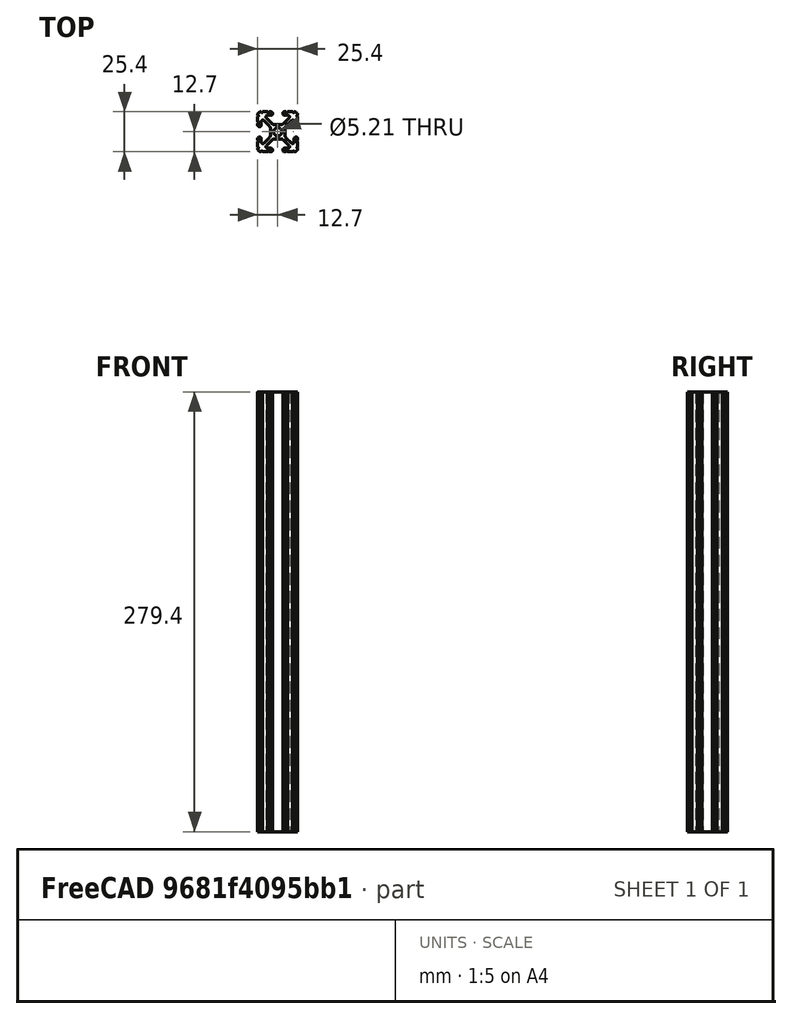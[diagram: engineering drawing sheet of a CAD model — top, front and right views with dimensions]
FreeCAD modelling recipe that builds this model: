
FCSTD DOCUMENT  (FreeCAD 0.19R24267 (Git))
Label: 1010-11
License: All rights reserved
LicenseURL: http://en.wikipedia.org/wiki/All_rights_reserved
objects: Sketcher::SketchObject×1, Part::Extrusion×1
note: 2 computed .brp shape members not serialized (recipe doc carries the construction recipe); baked Part::Feature solids carry a one-line shape summary decoded from their .brp

FEATURE [Sketcher::SketchObject] Sketch097
  FullyConstrained = false
  sketch-geometry (97):
    g0: Circle CenterX=0 CenterY=0 CenterZ=0 NormalX=0 NormalY=0 NormalZ=-1 AngleXU=0 Radius=2.6035
    g1: ArcOfCircle CenterX=12.7 CenterY=5.82508 CenterZ=0 NormalX=0 NormalY=0 NormalZ=1 AngleXU=0 Radius=0.508 StartAngle=1.5708 EndAngle=4.71239
    g2: LineSegment StartX=3.2385 StartY=11.651 StartZ=0 EndX=3.2385 EndY=11.5392 EndZ=0
    g3: LineSegment StartX=6.33313 StartY=-12.7 StartZ=0 EndX=9.55044 EndY=-12.7 EndZ=0
    g4: LineSegment StartX=7.20704 StartY=8.72437 StartZ=0 EndX=3.89827 EndY=5.42317 EndZ=0
    g5: ArcOfCircle CenterX=7.6835 CenterY=1.59319 CenterZ=0 NormalX=0 NormalY=0 NormalZ=1 AngleXU=0 Radius=3.175 StartAngle=2.35505 EndAngle=3.14159
    g6: ArcOfCircle CenterX=-1.70925 CenterY=-7.6708 CenterZ=0 NormalX=0 NormalY=0 NormalZ=1 AngleXU=0 Radius=3.175 StartAngle=1.5708 EndAngle=2.35528
    g7: ArcOfCircle CenterX=11.5392 CenterY=-4.28747 CenterZ=0 NormalX=0 NormalY=0 NormalZ=1 AngleXU=0 Radius=1.04901 StartAngle=1.5708 EndAngle=3.14159
    g8: ArcOfCircle CenterX=12.7 CenterY=-5.82508 CenterZ=0 NormalX=0 NormalY=0 NormalZ=1 AngleXU=0 Radius=0.508 StartAngle=1.5708 EndAngle=4.71239
    g9: LineSegment StartX=4.28751 StartY=10.4902 StartZ=0 EndX=6.47679 EndY=10.4902 EndZ=0
    g10: ArcOfCircle CenterX=4.28751 CenterY=11.651 CenterZ=0 NormalX=0 NormalY=0 NormalZ=1 AngleXU=0 Radius=1.04901 StartAngle=1.5708 EndAngle=3.14159
    g11: ArcOfCircle CenterX=6.47679 CenterY=9.45629 CenterZ=0 NormalX=0 NormalY=0 NormalZ=1 AngleXU=0 Radius=1.03391 StartAngle=5.49664 EndAngle=7.85398
    g12: ArcOfCircle CenterX=4.28751 CenterY=11.5392 CenterZ=0 NormalX=0 NormalY=0 NormalZ=1 AngleXU=0 Radius=1.04901 StartAngle=3.14159 EndAngle=4.71239
    g13: LineSegment StartX=3.95227 StartY=-5.42369 StartZ=0 EndX=7.17965 EndY=-8.64519 EndZ=0
    g14: ArcOfCircle CenterX=11.651 CenterY=4.28747 CenterZ=0 NormalX=0 NormalY=0 NormalZ=1 AngleXU=0 Radius=1.04901 StartAngle=4.71239 EndAngle=6.28319
    g15: ArcOfCircle CenterX=-5.82513 CenterY=-12.7 CenterZ=0 NormalX=0 NormalY=0 NormalZ=1 AngleXU=0 Radius=0.508 StartAngle=0 EndAngle=3.14159
    g16: LineSegment StartX=-6.47679 StartY=10.4902 StartZ=0 EndX=-4.28751 EndY=10.4902 EndZ=0
    g17: ArcOfCircle CenterX=-12.7 CenterY=10.0584 CenterZ=0 NormalX=0 NormalY=0 NormalZ=1 AngleXU=0 Radius=0.508 StartAngle=4.71239 EndAngle=7.85368
    g18: ArcOfCircle CenterX=-12.7 CenterY=5.82508 CenterZ=0 NormalX=0 NormalY=0 NormalZ=1 AngleXU=0 Radius=0.508 StartAngle=4.71239 EndAngle=7.85398
    g19: LineSegment StartX=-11.5392 StartY=-3.23846 StartZ=0 EndX=-11.651 EndY=-3.23846 EndZ=0
    g20: LineSegment StartX=-3.89827 StartY=5.42317 StartZ=0 EndX=-7.20704 EndY=8.72437 EndZ=0
    g21: LineSegment StartX=1.65578 StartY=4.4958 StartZ=0 EndX=-1.65578 EndY=4.4958 EndZ=0
    g22: ArcOfCircle CenterX=-1.65578 CenterY=7.6708 CenterZ=0 NormalX=0 NormalY=0 NormalZ=1 AngleXU=0 Radius=3.175 StartAngle=3.92813 EndAngle=4.71239
    g23: LineSegment StartX=-9.55044 StartY=-12.7 StartZ=0 EndX=-6.33313 EndY=-12.7 EndZ=0
    g24: ArcOfCircle CenterX=-5.82513 CenterY=12.7 CenterZ=0 NormalX=0 NormalY=0 NormalZ=1 AngleXU=0 Radius=0.508 StartAngle=3.14159 EndAngle=6.28319
    g25: ArcOfCircle CenterX=-4.28751 CenterY=11.651 CenterZ=0 NormalX=0 NormalY=0 NormalZ=1 AngleXU=0 Radius=1.04901 StartAngle=0 EndAngle=1.5708
    g26: LineSegment StartX=-12.7 StartY=-4.28747 StartZ=0 EndX=-12.7 EndY=-5.31708 EndZ=0
    g27: ArcOfCircle CenterX=-6.47679 CenterY=9.45629 CenterZ=0 NormalX=0 NormalY=0 NormalZ=1 AngleXU=0 Radius=1.03391 StartAngle=1.5708 EndAngle=3.92813
    g28: ArcOfCircle CenterX=-4.28751 CenterY=11.5392 CenterZ=0 NormalX=0 NormalY=0 NormalZ=1 AngleXU=0 Radius=1.04901 StartAngle=4.71239 EndAngle=6.28319
    g29: LineSegment StartX=-5.44101 StartY=-3.84082 StartZ=0 EndX=-8.73713 EndY=-7.12941 EndZ=0
    g30: ArcOfCircle CenterX=-7.6835 CenterY=-1.59319 CenterZ=0 NormalX=0 NormalY=0 NormalZ=1 AngleXU=0 Radius=3.175 StartAngle=5.49664 EndAngle=6.28319
    g31: LineSegment StartX=-12.7 StartY=5.31708 StartZ=0 EndX=-12.7 EndY=4.28747 EndZ=0
    g32: LineSegment StartX=-8.73713 StartY=7.12941 StartZ=0 EndX=-5.44101 EndY=3.84082 EndZ=0
    g33: LineSegment StartX=-11.651 StartY=3.23846 StartZ=0 EndX=-11.5392 EndY=3.23846 EndZ=0
    g34: ArcOfCircle CenterX=-9.46279 CenterY=-6.40209 CenterZ=0 NormalX=0 NormalY=0 NormalZ=1 AngleXU=0 Radius=1.02741 StartAngle=3.14159 EndAngle=5.49664
    g35: ArcOfCircle CenterX=-10.5918 CenterY=10.5918 CenterZ=0 NormalX=0 NormalY=0 NormalZ=1 AngleXU=0 Radius=2.1082 StartAngle=1.55877 EndAngle=3.15364
    g36: LineSegment StartX=-12.7 StartY=9.5504 StartZ=0 EndX=-12.7 EndY=6.33308 EndZ=0
    g37: LineSegment StartX=-6.33313 StartY=12.7 StartZ=0 EndX=-9.55044 EndY=12.7 EndZ=0
    g38: ArcOfCircle CenterX=-11.5392 CenterY=-4.28747 CenterZ=0 NormalX=0 NormalY=0 NormalZ=1 AngleXU=0 Radius=1.04901 StartAngle=0 EndAngle=1.5708
    g39: LineSegment StartX=4.28751 StartY=-12.7 StartZ=0 EndX=5.31713 EndY=-12.7 EndZ=0
    g40: LineSegment StartX=5.44101 StartY=3.84082 StartZ=0 EndX=8.73713 EndY=7.12941 EndZ=0
    g41: LineSegment StartX=10.4902 StartY=-4.28747 StartZ=0 EndX=10.4902 EndY=-6.40209 EndZ=0
    g42: ArcOfCircle CenterX=9.46279 CenterY=6.40209 CenterZ=0 NormalX=0 NormalY=0 NormalZ=1 AngleXU=0 Radius=1.02741 StartAngle=0 EndAngle=2.35505
    g43: ArcOfCircle CenterX=5.82513 CenterY=-12.7 CenterZ=0 NormalX=0 NormalY=0 NormalZ=1 AngleXU=0 Radius=0.508 StartAngle=0 EndAngle=3.14159
    g44: LineSegment StartX=12.7 StartY=-9.5504 StartZ=0 EndX=12.7 EndY=-6.33308 EndZ=0
    g45: LineSegment StartX=4.5085 StartY=-1.59319 StartZ=0 EndX=4.5085 EndY=1.59319 EndZ=0
    g46: ArcOfCircle CenterX=12.7 CenterY=10.0584 CenterZ=0 NormalX=0 NormalY=0 NormalZ=1 AngleXU=0 Radius=0.508 StartAngle=1.5711 EndAngle=4.71239
    g47: ArcOfCircle CenterX=12.7 CenterY=-10.0584 CenterZ=0 NormalX=0 NormalY=0 NormalZ=1 AngleXU=0 Radius=0.508 StartAngle=1.5708 EndAngle=4.71209
    g48: LineSegment StartX=3.2385 StartY=-11.5392 StartZ=0 EndX=3.2385 EndY=-11.651 EndZ=0
    g49: LineSegment StartX=8.73713 StartY=-7.12941 StartZ=0 EndX=5.44101 EndY=-3.84082 EndZ=0
    g50: ArcOfCircle CenterX=11.651 CenterY=-4.28747 CenterZ=0 NormalX=0 NormalY=0 NormalZ=1 AngleXU=0 Radius=1.04901 StartAngle=0 EndAngle=1.5708
    g51: ArcOfCircle CenterX=1.65578 CenterY=7.6708 CenterZ=0 NormalX=0 NormalY=0 NormalZ=1 AngleXU=0 Radius=3.175 StartAngle=4.71239 EndAngle=5.49664
    g52: ArcOfCircle CenterX=7.6835 CenterY=-1.59319 CenterZ=0 NormalX=0 NormalY=0 NormalZ=1 AngleXU=0 Radius=3.175 StartAngle=3.14159 EndAngle=3.92813
    g53: LineSegment StartX=12.7 StartY=4.28747 StartZ=0 EndX=12.7 EndY=5.31708 EndZ=0
    g54: ArcOfCircle CenterX=6.41641 CenterY=-9.40983 CenterZ=0 NormalX=0 NormalY=0 NormalZ=1 AngleXU=0 Radius=1.08037 StartAngle=4.71239 EndAngle=7.06949
    g55: LineSegment StartX=12.7 StartY=-5.31708 StartZ=0 EndX=12.7 EndY=-4.28747 EndZ=0
    g56: ArcOfCircle CenterX=10.0584 CenterY=-12.7 CenterZ=0 NormalX=0 NormalY=0 NormalZ=1 AngleXU=0 Radius=0.508 StartAngle=0.000300194 EndAngle=3.14159
    g57: ArcOfCircle CenterX=11.5392 CenterY=4.28747 CenterZ=0 NormalX=0 NormalY=0 NormalZ=1 AngleXU=0 Radius=1.04901 StartAngle=3.14159 EndAngle=4.71239
    g58: LineSegment StartX=12.7 StartY=6.33308 StartZ=0 EndX=12.7 EndY=9.5504 EndZ=0
    g59: ArcOfCircle CenterX=4.28751 CenterY=-11.5392 CenterZ=0 NormalX=0 NormalY=0 NormalZ=1 AngleXU=0 Radius=1.04901 StartAngle=1.5708 EndAngle=3.14159
    g60: ArcOfCircle CenterX=10.5918 CenterY=10.5918 CenterZ=0 NormalX=0 NormalY=0 NormalZ=1 AngleXU=0 Radius=2.1082 StartAngle=6.27114 EndAngle=7.86601
    g61: ArcOfCircle CenterX=9.46279 CenterY=-6.40209 CenterZ=0 NormalX=0 NormalY=0 NormalZ=1 AngleXU=0 Radius=1.02741 StartAngle=3.92813 EndAngle=6.28319
    g62: LineSegment StartX=6.41641 StartY=-10.4902 StartZ=0 EndX=4.28751 EndY=-10.4902 EndZ=0
    g63: LineSegment StartX=-10.4902 StartY=-6.40209 StartZ=0 EndX=-10.4902 EndY=-4.28747 EndZ=0
    g64: ArcOfCircle CenterX=-9.46279 CenterY=6.40209 CenterZ=0 NormalX=0 NormalY=0 NormalZ=1 AngleXU=0 Radius=1.02741 StartAngle=0.786542 EndAngle=3.14159
    g65: LineSegment StartX=-10.4902 StartY=4.28747 StartZ=0 EndX=-10.4902 EndY=6.40209 EndZ=0
    g66: LineSegment StartX=-4.5085 StartY=1.59319 StartZ=0 EndX=-4.5085 EndY=-1.59319 EndZ=0
    g67: LineSegment StartX=-4.28751 StartY=12.7 StartZ=0 EndX=-5.31713 EndY=12.7 EndZ=0
    g68: ArcOfCircle CenterX=-11.5392 CenterY=4.28747 CenterZ=0 NormalX=0 NormalY=0 NormalZ=1 AngleXU=0 Radius=1.04901 StartAngle=4.71239 EndAngle=6.28319
    g69: LineSegment StartX=-3.2385 StartY=11.5392 StartZ=0 EndX=-3.2385 EndY=11.651 EndZ=0
    g70: ArcOfCircle CenterX=-11.651 CenterY=4.28747 CenterZ=0 NormalX=0 NormalY=0 NormalZ=1 AngleXU=0 Radius=1.04901 StartAngle=3.14159 EndAngle=4.71239
    g71: ArcOfCircle CenterX=-7.6835 CenterY=1.59319 CenterZ=0 NormalX=0 NormalY=0 NormalZ=1 AngleXU=0 Radius=3.175 StartAngle=0 EndAngle=0.786542
    g72: ArcOfCircle CenterX=-10.0584 CenterY=12.7 CenterZ=0 NormalX=0 NormalY=0 NormalZ=1 AngleXU=0 Radius=0.508 StartAngle=3.14189 EndAngle=6.28319
    g73: LineSegment StartX=-1.70925 StartY=-4.4958 StartZ=0 EndX=1.70925 EndY=-4.4958 EndZ=0
    g74: LineSegment StartX=11.651 StartY=-3.23846 StartZ=0 EndX=11.5392 EndY=-3.23846 EndZ=0
    g75: ArcOfCircle CenterX=-10.5918 CenterY=-10.5918 CenterZ=0 NormalX=0 NormalY=0 NormalZ=1 AngleXU=0 Radius=2.1082 StartAngle=3.12954 EndAngle=4.72442
    g76: ArcOfCircle CenterX=10.5918 CenterY=-10.5918 CenterZ=0 NormalX=0 NormalY=0 NormalZ=1 AngleXU=0 Radius=2.1082 StartAngle=4.70036 EndAngle=6.29523
    g77: ArcOfCircle CenterX=-12.7 CenterY=-5.82508 CenterZ=0 NormalX=0 NormalY=0 NormalZ=1 AngleXU=0 Radius=0.508 StartAngle=4.71239 EndAngle=7.85398
    g78: ArcOfCircle CenterX=5.82513 CenterY=12.7 CenterZ=0 NormalX=0 NormalY=0 NormalZ=1 AngleXU=0 Radius=0.508 StartAngle=3.14159 EndAngle=6.28319
    g79: LineSegment StartX=9.55044 StartY=12.7 StartZ=0 EndX=6.33313 EndY=12.7 EndZ=0
    g80: ArcOfCircle CenterX=10.0584 CenterY=12.7 CenterZ=0 NormalX=0 NormalY=0 NormalZ=1 AngleXU=0 Radius=0.508 StartAngle=3.14159 EndAngle=6.28289
    g81: ArcOfCircle CenterX=1.70925 CenterY=-7.6708 CenterZ=0 NormalX=0 NormalY=0 NormalZ=1 AngleXU=0 Radius=3.175 StartAngle=0.78631 EndAngle=1.5708
    g82: ArcOfCircle CenterX=4.28751 CenterY=-11.651 CenterZ=0 NormalX=0 NormalY=0 NormalZ=1 AngleXU=0 Radius=1.04901 StartAngle=3.14159 EndAngle=4.71239
    g83: LineSegment StartX=5.31713 StartY=12.7 StartZ=0 EndX=4.28751 EndY=12.7 EndZ=0
    g84: LineSegment StartX=10.4902 StartY=6.40209 StartZ=0 EndX=10.4902 EndY=4.28747 EndZ=0
    g85: LineSegment StartX=11.5392 StartY=3.23846 StartZ=0 EndX=11.651 EndY=3.23846 EndZ=0
    g86: ArcOfCircle CenterX=-10.0584 CenterY=-12.7 CenterZ=0 NormalX=0 NormalY=0 NormalZ=1 AngleXU=0 Radius=0.508 StartAngle=0 EndAngle=3.14129
    g87: ArcOfCircle CenterX=-12.7 CenterY=-10.0584 CenterZ=0 NormalX=0 NormalY=0 NormalZ=1 AngleXU=0 Radius=0.508 StartAngle=4.71269 EndAngle=7.85398
    g88: ArcOfCircle CenterX=-4.28751 CenterY=-11.5392 CenterZ=0 NormalX=0 NormalY=0 NormalZ=1 AngleXU=0 Radius=1.04901 StartAngle=0 EndAngle=1.5708
    g89: ArcOfCircle CenterX=-4.28751 CenterY=-11.651 CenterZ=0 NormalX=0 NormalY=0 NormalZ=1 AngleXU=0 Radius=1.04901 StartAngle=4.71239 EndAngle=6.28319
    g90: LineSegment StartX=-12.7 StartY=-6.33308 StartZ=0 EndX=-12.7 EndY=-9.5504 EndZ=0
    g91: ArcOfCircle CenterX=-11.651 CenterY=-4.28747 CenterZ=0 NormalX=0 NormalY=0 NormalZ=1 AngleXU=0 Radius=1.04901 StartAngle=1.5708 EndAngle=3.14159
    g92: LineSegment StartX=-7.17965 StartY=-8.64519 StartZ=0 EndX=-3.95227 EndY=-5.42369 EndZ=0
    g93: LineSegment StartX=-5.31713 StartY=-12.7 StartZ=0 EndX=-4.28751 EndY=-12.7 EndZ=0
    g94: LineSegment StartX=-3.2385 StartY=-11.651 StartZ=0 EndX=-3.2385 EndY=-11.5392 EndZ=0
    g95: ArcOfCircle CenterX=-6.41641 CenterY=-9.40983 CenterZ=0 NormalX=0 NormalY=0 NormalZ=1 AngleXU=0 Radius=1.08037 StartAngle=2.35528 EndAngle=4.71239
    g96: LineSegment StartX=-4.28751 StartY=-10.4902 StartZ=0 EndX=-6.41641 EndY=-10.4902 EndZ=0
FEATURE [Part::Extrusion] Extrude
  Base = -> Sketch097
  Dir = (0,0,1)
  DirMode = 2
  FaceMakerClass = Part::FaceMakerBullseye
  LengthFwd = 279.4
  LengthRev = 0
  Solid = true
  Symmetric = false
